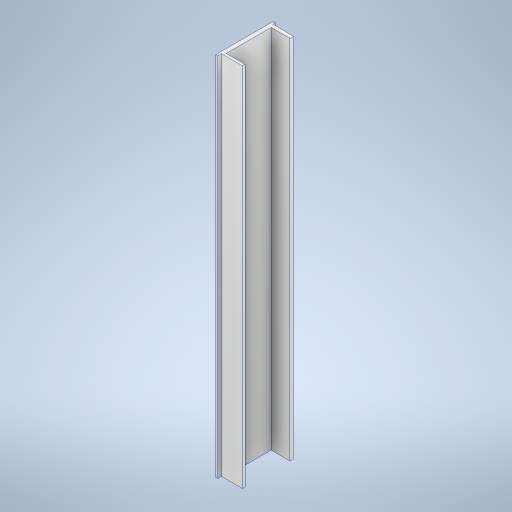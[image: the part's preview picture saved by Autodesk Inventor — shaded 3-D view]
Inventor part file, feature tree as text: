
AUTODESK INVENTOR PART (.ipt)
format: ipt  version: 2024 (Build 280153000, 153)  size: 254,976 bytes
history: native  units: mm
features: extrude x1, sketch x1
ambient origin geometry x8: Origin, YZ Plane, XZ Plane, XY Plane, X Axis, Y Axis, Z Axis, Center Point
bodies: Solid1 (feature_tree)
feature tree (2):
  extrude  "Extrusion1"  Depth=700.0mm TaperAngle=0.0deg
  sketch  "Sketch1"  dims[d0=110.0mm d1=700.0mm d2=0.0mm]
